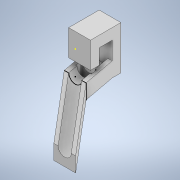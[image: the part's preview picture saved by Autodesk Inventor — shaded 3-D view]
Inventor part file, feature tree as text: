
AUTODESK INVENTOR PART (.ipt)
format: ipt  version: 2021 (Build 250183000, 183)  size: 216,064 bytes
history: native  units: mm
features: sketch x12, extrude x6, plane x3, sweep x1, thread x1, loft x1, other x1
ambient origin geometry x8: Origin, YZ Plane, XZ Plane, XY Plane, X Axis, Y Axis, Z Axis, Center Point
bodies: Solid1 (feature_tree)
feature tree (25):
  extrude  "Extrusion1"  Depth=50.0mm
  extrude  "Extrusion2"  Depth=12.5mm
  extrude  "Extrusion3"  Depth=10.0mm
  extrude  "Extrusion4"  Depth=6.0mm TaperAngle=0.0deg
  extrude  "Extrusion5"  Depth=15.0mm TaperAngle=0.0deg
  sketch  "Sketch6"  dims[d14=25.0mm d15=10.0mm d16=0.0mm d17=15.0mm]
  plane  "Work Plane1"
  sweep  "Sweep1"
  thread  "Thread1"  [1 undecoded]
  sketch  "Sketch9"  dims[d21=30.0mm d22=15.0mm]
  sketch  "Sketch10"  dims[d23=17.0mm]
  plane  "Work Plane2"
  extrude  "Extrusion6"  Depth=10.0mm TaperAngle=0.0deg
  sketch  "Sketch13"  dims[d25=-12.5mm]
  plane  "Work Plane3"
  loft  "Loft1"
  sketch  "Sketch1"  dims[d0=25.0mm d1=50.0mm]
  sketch  "Sketch2"  dims[d2=12.5mm d3=12.5mm]
  sketch  "Sketch3"  dims[d4=10.0mm d5=0.0mm d7=3.0mm]
  sketch  "Sketch4"  dims[d8=33.0mm d9=6.0mm d10=0.0mm]
  sketch  "Sketch5"  dims[d11=15.0mm d12=15.0mm d13=0.0mm]
  sketch  "Sketch8"  dims[d18=15.0mm d19=10.0mm d20=0.0mm]
  sketch  "Sketch12"  dims[d24=17.0mm]
  sketch  "Sketch14"  dims[d26=2.268928mm d27=8.5mm d28=0.0mm d29=0.0mm d30=6.0mm d31=0.0mm d32=30.0mm d33=18.0mm d34=6.0mm d35=3.5mm d36=14.5mm d37=25.0mm d38=0.0mm d39=40.0mm d40=17.0mm d41=25.0mm d42=5.0mm d43=5.0mm d45=15.0mm d46=38.574mm d47=28.0mm d48=0.0mm d49=90.0deg d50=0.0mm d51=90.0deg]
  other  "Edges1"
note: 1 required parameter value undecoded (feature->parameter linkage not recoverable at this tier; creation-order binding heuristic only, values carry confidence <= 0.55)
